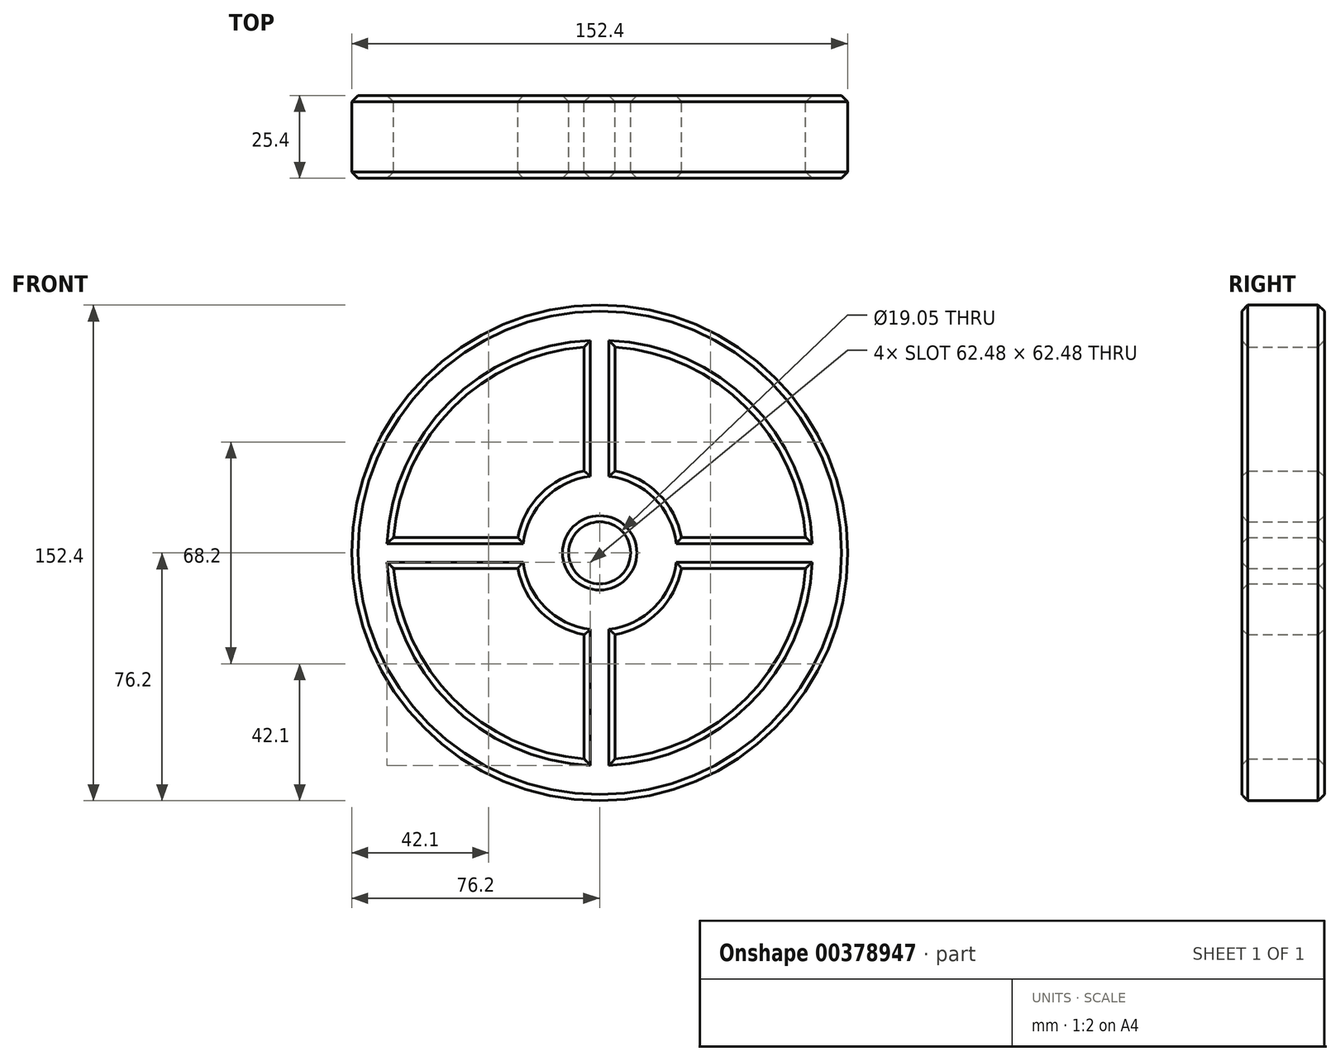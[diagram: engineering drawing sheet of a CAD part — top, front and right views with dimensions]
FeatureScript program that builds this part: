
annotation { "Feature Type Name" : "Feature", "Feature Type Description" : "" }
export const myFeature = defineFeature(function(context is Context, id is Id, definition is map)
    precondition{}
    {
        {
            var Q0;
            Q0=qCreatedBy(makeId("Front.planeOp"),FACE);
            var sketch = newSketch(context, id + "F0", { "sketchPlane" : qUnion([Q0])});
            skCircle(sketch, "E0", {"center": v(0, 0) * mm, "radius": 76.2 * mm});
            skArc(sketch, "E1", {"start": v(-63.32, -4.76) * mm, "mid": v(-44.9, -44.9) * mm, "end": v(-4.76, -63.32) * mm});
            skLineSegment(sketch, "E2", {"start": v(-4.76, 63.32) * mm, "end": v(-4.76, 6.35) * mm});
            skLineSegment(sketch, "E3", {"start": v(4.76, -63.32) * mm, "end": v(4.76, -6.35) * mm});
            skLineSegment(sketch, "E4", {"start": v(-63.32, 4.76) * mm, "end": v(-6.35, 4.76) * mm});
            skLineSegment(sketch, "E5", {"start": v(63.32, -4.76) * mm, "end": v(6.35, -4.76) * mm});
            skArc(sketch, "E6.trimOffspring", {"start": v(63.32, 4.76) * mm, "mid": v(44.9, 44.9) * mm, "end": v(4.76, 63.32) * mm});
            skArc(sketch, "E7.trimOffspring", {"start": v(-4.76, 63.32) * mm, "mid": v(-44.9, 44.9) * mm, "end": v(-63.32, 4.76) * mm});
            skArc(sketch, "E8.trimOffspring", {"start": v(4.76, -63.32) * mm, "mid": v(44.9, -44.9) * mm, "end": v(63.32, -4.76) * mm});
            skPoint(sketch, "E9.orphan", {"position": v(-4.76, -76.05) * mm});
            skPoint(sketch, "E10.orphan", {"position": v(4.76, -76.05) * mm});
            skLineSegment(sketch, "E11.trimOffspring", {"start": v(-4.76, -6.35) * mm, "end": v(-4.76, -63.32) * mm});
            skLineSegment(sketch, "E12.trimOffspring", {"start": v(6.35, 4.76) * mm, "end": v(63.32, 4.76) * mm});
            skLineSegment(sketch, "E13.trimOffspring", {"start": v(4.76, 6.35) * mm, "end": v(4.76, 63.32) * mm});
            skLineSegment(sketch, "E14", {"start": v(6.35, -4.76) * mm, "end": v(-63.32, -4.76) * mm});
            skLineSegment(sketch, "E15", {"start": v(-4.76, -6.35) * mm, "end": v(-4.76, 6.35) * mm});
            skLineSegment(sketch, "E16", {"start": v(6.35, 4.76) * mm, "end": v(-6.35, 4.76) * mm});
            skLineSegment(sketch, "E17", {"start": v(4.76, -6.35) * mm, "end": v(4.76, 6.35) * mm});
            skArc(sketch, "E18", {"start": v(-25.16, -4.76) * mm, "mid": v(-18.1, -18.1) * mm, "end": v(-4.76, -25.16) * mm});
            skCircle(sketch, "E19", {"center": v(0, 0) * mm, "radius": 9.53 * mm});
            skArc(sketch, "E20.trimOffspring", {"start": v(-4.76, 25.16) * mm, "mid": v(-18.1, 18.1) * mm, "end": v(-25.16, 4.76) * mm});
            skArc(sketch, "E21.trimOffspring", {"start": v(25.16, 4.76) * mm, "mid": v(18.1, 18.1) * mm, "end": v(4.76, 25.16) * mm});
            skArc(sketch, "E22.trimOffspring", {"start": v(4.76, -25.16) * mm, "mid": v(18.1, -18.1) * mm, "end": v(25.16, -4.76) * mm});
            skSolve(sketch);
        }
        {
            var Q0;
            Q0 = qSketchRegion(id + "F0", true);
            var Q1;
            {var subQ0=sQuery(id+"F0.wireOp",EDGE,"E20.trimOffspring");Q1=makeQuery(id+"F0.imprint","IMPRINT",FACE,{"disambiguationData":[TD([[makeQuery(id+"F0.imprint","IMPRINT",EDGE,{"derivedFrom":subQ0}),1.0]])]});}
            var Q2;
            {var subQ0=sQuery(id+"F0.wireOp",EDGE,"E21.trimOffspring");Q2=makeQuery(id+"F0.imprint","IMPRINT",FACE,{"disambiguationData":[TD([[makeQuery(id+"F0.imprint","IMPRINT",EDGE,{"derivedFrom":subQ0}),1.0]])]});}
            var Q3;
            {var subQ0=sQuery(id+"F0.wireOp",EDGE,"E22.trimOffspring");Q3=makeQuery(id+"F0.imprint","IMPRINT",FACE,{"disambiguationData":[TD([[makeQuery(id+"F0.imprint","IMPRINT",EDGE,{"derivedFrom":subQ0}),1.0]])]});}
            var Q4;
            {var subQ0=sQuery(id+"F0.wireOp",EDGE,"E18");Q4=makeQuery(id+"F0.imprint","IMPRINT",FACE,{"disambiguationData":[TD([[makeQuery(id+"F0.imprint","IMPRINT",EDGE,{"derivedFrom":subQ0}),1.0]])]});}
            extrude(context, id + "F1", {"entities" : qUnion([Q0, Q1, Q2, Q3, Q4]), "endBound" : BoundingType.SYMMETRIC, "depth" : 25.4 * mm});
        }
        {
            var Q0;
            Q0=makeQuery(id+"F1.opExtrude","CAP_FACE",FACE,{"disambiguationData":[OSD([sQuery(id+"F0.wireOp",EDGE,"E0"),sQuery(id+"F0.wireOp",EDGE,"E1"),sQuery(id+"F0.wireOp",EDGE,"E2"),sQuery(id+"F0.wireOp",EDGE,"E3"),sQuery(id+"F0.wireOp",EDGE,"E4"),sQuery(id+"F0.wireOp",EDGE,"E5"),sQuery(id+"F0.wireOp",EDGE,"E6.trimOffspring"),sQuery(id+"F0.wireOp",EDGE,"E7.trimOffspring"),sQuery(id+"F0.wireOp",EDGE,"E8.trimOffspring"),sQuery(id+"F0.wireOp",EDGE,"E11.trimOffspring"),sQuery(id+"F0.wireOp",EDGE,"E12.trimOffspring"),sQuery(id+"F0.wireOp",EDGE,"E13.trimOffspring"),sQuery(id+"F0.wireOp",EDGE,"E14"),sQuery(id+"F0.wireOp",EDGE,"E18"),sQuery(id+"F0.wireOp",EDGE,"E19"),sQuery(id+"F0.wireOp",EDGE,"E20.trimOffspring"),sQuery(id+"F0.wireOp",EDGE,"E21.trimOffspring"),sQuery(id+"F0.wireOp",EDGE,"E22.trimOffspring")])],"isStart":false});
            chamfer(context, id + "F2", {"entities" : qUnion([Q0]), "width" : 1.9 * mm, "tangentPropagation" : true});
        }
        {
            var Q0;
            Q0=makeQuery(id+"F1.opExtrude","CAP_FACE",FACE,{"disambiguationData":[OSD([sQuery(id+"F0.wireOp",EDGE,"E0"),sQuery(id+"F0.wireOp",EDGE,"E1"),sQuery(id+"F0.wireOp",EDGE,"E2"),sQuery(id+"F0.wireOp",EDGE,"E3"),sQuery(id+"F0.wireOp",EDGE,"E4"),sQuery(id+"F0.wireOp",EDGE,"E5"),sQuery(id+"F0.wireOp",EDGE,"E6.trimOffspring"),sQuery(id+"F0.wireOp",EDGE,"E7.trimOffspring"),sQuery(id+"F0.wireOp",EDGE,"E8.trimOffspring"),sQuery(id+"F0.wireOp",EDGE,"E11.trimOffspring"),sQuery(id+"F0.wireOp",EDGE,"E12.trimOffspring"),sQuery(id+"F0.wireOp",EDGE,"E13.trimOffspring"),sQuery(id+"F0.wireOp",EDGE,"E14"),sQuery(id+"F0.wireOp",EDGE,"E18"),sQuery(id+"F0.wireOp",EDGE,"E19"),sQuery(id+"F0.wireOp",EDGE,"E20.trimOffspring"),sQuery(id+"F0.wireOp",EDGE,"E21.trimOffspring"),sQuery(id+"F0.wireOp",EDGE,"E22.trimOffspring")])],"isStart":true});
            chamfer(context, id + "F3", {"entities" : qUnion([Q0]), "width" : 1.9 * mm, "tangentPropagation" : true});
        }
    });
